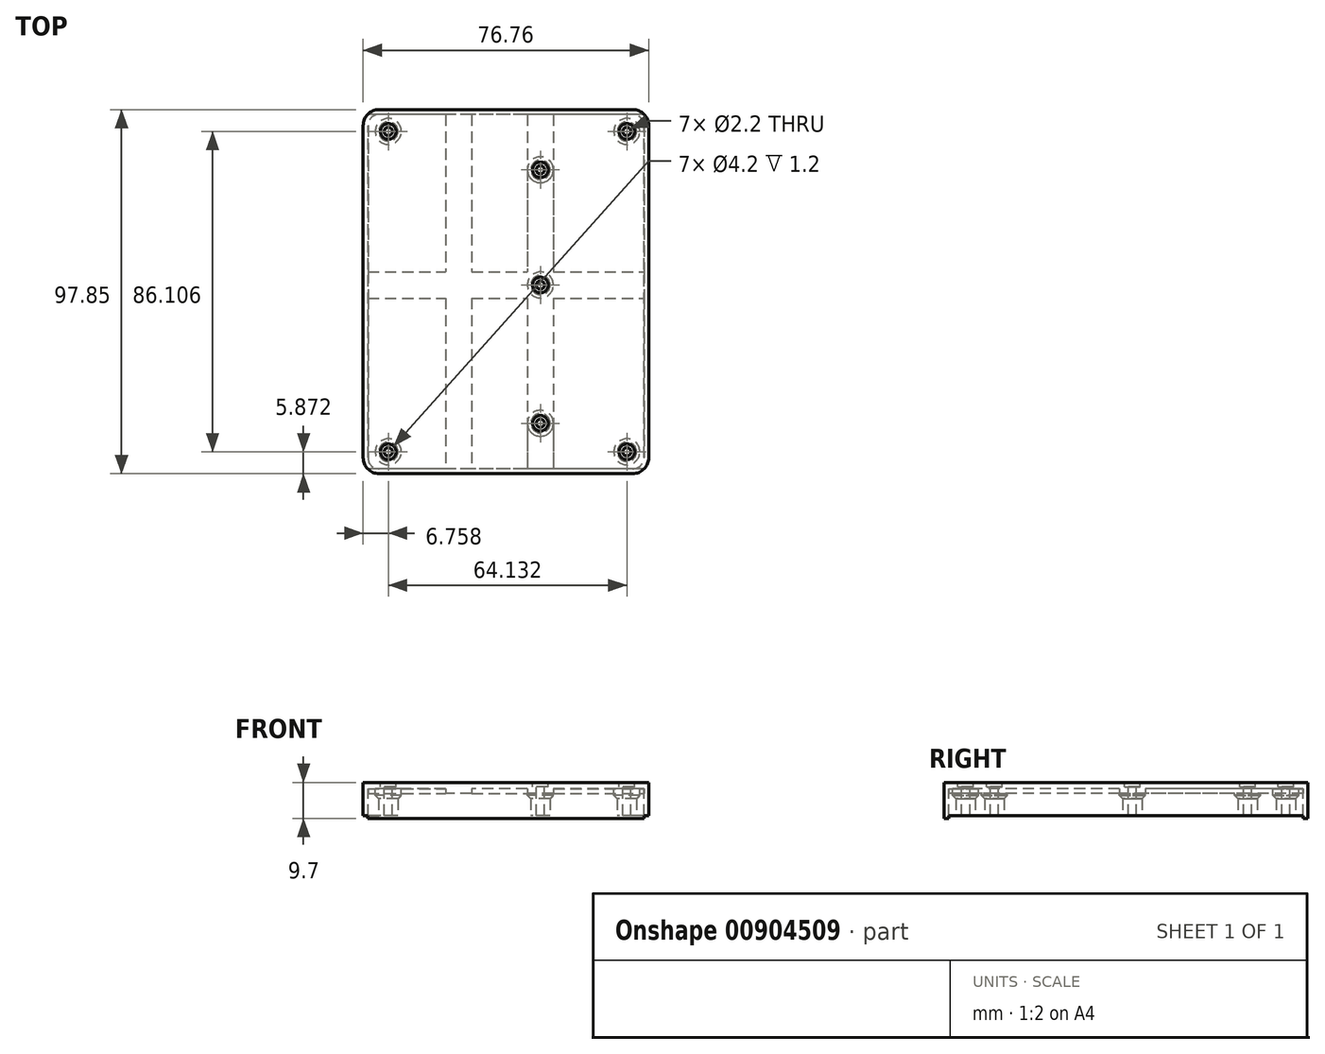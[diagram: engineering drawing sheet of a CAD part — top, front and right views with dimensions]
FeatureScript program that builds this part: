
annotation { "Feature Type Name" : "Feature", "Feature Type Description" : "" }
export const myFeature = defineFeature(function(context is Context, id is Id, definition is map)
    precondition{}
    {
        {
            var Q0;
            Q0=qCreatedBy(makeId("Right.planeOp"),FACE);
            cPlane(context, id + "F0", {"entities" : qUnion([Q0]), "cplaneType" : CPlaneType.OFFSET, "offset" : 9.15 * mm, "width" : 150 * mm, "height" : 150 * mm});
        }
        {
            var Q0;
            Q0=qCreatedBy(makeId("Right.planeOp"),FACE);
            cPlane(context, id + "F1", {"entities" : qUnion([Q0]), "cplaneType" : CPlaneType.OFFSET, "offset" : 83.31 * mm, "width" : 150 * mm, "height" : 150 * mm});
        }
        {
            var Q0;
            Q0=qCreatedBy(makeId("Front.planeOp"),FACE);
            cPlane(context, id + "F2", {"entities" : qUnion([Q0]), "cplaneType" : CPlaneType.OFFSET, "offset" : 95.25 * mm, "oppositeDirection" : true, "width" : 150 * mm, "height" : 150 * mm});
        }
        {
            var Q0;
            Q0=qCreatedBy(makeId("Top.planeOp"),FACE);
            cPlane(context, id + "F3", {"entities" : qUnion([Q0]), "cplaneType" : CPlaneType.OFFSET, "offset" : 1.7 * mm, "width" : 150 * mm, "height" : 150 * mm});
        }
        {
            var Q0;
            Q0=qCreatedBy(id+"F3.planeOp",FACE);
            var sketch = newSketch(context, id + "F4", { "sketchPlane" : qUnion([Q0])});
            skLineSegment(sketch, "E0", {"start": v(83.31, 92.25) * mm, "end": v(83.31, 3) * mm, "construction": true});
            skLineSegment(sketch, "E1", {"start": v(80.31, 95.25) * mm, "end": v(12.15, 95.25) * mm, "construction": true});
            skLineSegment(sketch, "E2", {"start": v(9.15, 92.25) * mm, "end": v(9.15, 3) * mm, "construction": true});
            skLineSegment(sketch, "E3", {"start": v(80.31, 0) * mm, "end": v(12.15, 0) * mm, "construction": true});
            skPoint(sketch, "E4.visualSharp", {"position": v(83.31, 0) * mm});
            skArc(sketch, "E4.filletArc", {"start": v(80.31, 0) * mm, "mid": v(82.43, 0.88) * mm, "end": v(83.31, 3) * mm, "construction": true});
            skPoint(sketch, "E5.visualSharp", {"position": v(83.31, 95.25) * mm});
            skArc(sketch, "E5.filletArc", {"start": v(83.31, 92.25) * mm, "mid": v(82.43, 94.37) * mm, "end": v(80.31, 95.25) * mm, "construction": true});
            skPoint(sketch, "E6.visualSharp", {"position": v(9.15, 95.25) * mm});
            skArc(sketch, "E6.filletArc", {"start": v(12.15, 95.25) * mm, "mid": v(10.03, 94.37) * mm, "end": v(9.15, 92.25) * mm, "construction": true});
            skPoint(sketch, "E7.visualSharp", {"position": v(9.15, 0) * mm});
            skArc(sketch, "E7.filletArc", {"start": v(9.15, 3) * mm, "mid": v(10.03, 0.88) * mm, "end": v(12.15, 0) * mm, "construction": true});
            skArc(sketch, "E8.0", {"start": v(84.61, 92.25) * mm, "mid": v(83.35, 95.3) * mm, "end": v(80.31, 96.55) * mm});
            skLineSegment(sketch, "E8.1", {"start": v(80.31, 96.55) * mm, "end": v(12.15, 96.55) * mm});
            skLineSegment(sketch, "E8.2", {"start": v(84.61, 92.25) * mm, "end": v(84.61, 3) * mm});
            skArc(sketch, "E8.3", {"start": v(12.15, 96.55) * mm, "mid": v(9.1, 95.3) * mm, "end": v(7.85, 92.25) * mm});
            skArc(sketch, "E8.4", {"start": v(80.31, -1.3) * mm, "mid": v(83.35, -0.04) * mm, "end": v(84.61, 3) * mm});
            skLineSegment(sketch, "E8.5", {"start": v(80.31, -1.3) * mm, "end": v(12.15, -1.3) * mm});
            skArc(sketch, "E8.6", {"start": v(7.85, 3) * mm, "mid": v(9.1, -0.04) * mm, "end": v(12.15, -1.3) * mm});
            skLineSegment(sketch, "E8.7", {"start": v(7.85, 92.25) * mm, "end": v(7.85, 3) * mm});
            skSolve(sketch);
        }
        {
            var Q0;
            Q0=qCreatedBy(id+"F3.planeOp",FACE);
            cPlane(context, id + "F5", {"entities" : qUnion([Q0]), "cplaneType" : CPlaneType.OFFSET, "offset" : 5.9 * mm, "width" : 150 * mm, "height" : 150 * mm});
        }
        {
            var Q0;
            Q0=qCreatedBy(id+"F5.planeOp",FACE);
            cPlane(context, id + "F6", {"entities" : qUnion([Q0]), "cplaneType" : CPlaneType.OFFSET, "offset" : 3 * mm, "width" : 150 * mm, "height" : 150 * mm});
        }
        {
            var Q0;
            Q0=makeQuery(id+"F4.imprint","IMPRINT",FACE,{"disambiguationData":[TD([[makeQuery(id+"F4.imprint","IMPRINT",EDGE,{"derivedFrom":sQuery(id+"F4.wireOp",EDGE,"E8.0")}),1.0]])]});
            var Q1;
            Q1=qCreatedBy(id+"F6.planeOp",FACE);
            extrude(context, id + "F7", {"entities" : qUnion([Q0]), "endBound" : BoundingType.UP_TO_SURFACE, "depth" : 25 * mm, "endBoundEntityFace" : qUnion([Q1]), "offsetDistance" : 25 * mm});
        }
        {
            var Q0;
            Q0=qCreatedBy(id+"F3.planeOp",FACE);
            var sketch = newSketch(context, id + "F8", { "sketchPlane" : qUnion([Q0])});
            skLineSegment(sketch, "E9.0", {"start": v(83.31, 92.25) * mm, "end": v(83.31, 3) * mm});
            skArc(sketch, "E10.0", {"start": v(83.31, 92.25) * mm, "mid": v(82.43, 94.37) * mm, "end": v(80.31, 95.25) * mm});
            skLineSegment(sketch, "E11.0", {"start": v(80.31, 95.25) * mm, "end": v(12.15, 95.25) * mm});
            skArc(sketch, "E12.0", {"start": v(12.15, 95.25) * mm, "mid": v(10.03, 94.37) * mm, "end": v(9.15, 92.25) * mm});
            skLineSegment(sketch, "E13.0", {"start": v(9.15, 92.25) * mm, "end": v(9.15, 3) * mm});
            skArc(sketch, "E14.0", {"start": v(9.15, 3) * mm, "mid": v(10.03, 0.88) * mm, "end": v(12.15, 0) * mm});
            skLineSegment(sketch, "E15.0", {"start": v(80.31, 0) * mm, "end": v(12.15, 0) * mm});
            skArc(sketch, "E16.0", {"start": v(80.31, 0) * mm, "mid": v(82.43, 0.88) * mm, "end": v(83.31, 3) * mm});
            skLineSegment(sketch, "E17.0", {"start": v(84.61, 92.25) * mm, "end": v(84.61, 3) * mm});
            skArc(sketch, "E18.0", {"start": v(84.61, 92.25) * mm, "mid": v(83.35, 95.3) * mm, "end": v(80.31, 96.55) * mm});
            skLineSegment(sketch, "E19.0", {"start": v(80.31, 96.55) * mm, "end": v(12.15, 96.55) * mm});
            skArc(sketch, "E20.0", {"start": v(12.15, 96.55) * mm, "mid": v(9.1, 95.3) * mm, "end": v(7.85, 92.25) * mm});
            skLineSegment(sketch, "E21.0", {"start": v(7.85, 92.25) * mm, "end": v(7.85, 3) * mm});
            skArc(sketch, "E22.0", {"start": v(7.85, 3) * mm, "mid": v(9.1, -0.04) * mm, "end": v(12.15, -1.3) * mm});
            skLineSegment(sketch, "E23.0", {"start": v(80.31, -1.3) * mm, "end": v(12.15, -1.3) * mm});
            skArc(sketch, "E24.0", {"start": v(80.31, -1.3) * mm, "mid": v(83.35, -0.04) * mm, "end": v(84.61, 3) * mm});
            skSolve(sketch);
        }
        {
            var Q0;
            Q0=makeQuery(id+"F8.imprint","IMPRINT",FACE,{"disambiguationData":[TD([[makeQuery(id+"F8.imprint","IMPRINT",EDGE,{"derivedFrom":sQuery(id+"F8.wireOp",EDGE,"E9.0")}),1.0]])]});
            extrude(context, id + "F9", {"entities" : qUnion([Q0]), "operationType" : NewBodyOperationType.ADD, "oppositeDirection" : true, "depth" : 0.8 * mm, "offsetDistance" : 25 * mm});
        }
        {
            var Q0;
            Q0=qCreatedBy(id+"F3.planeOp",FACE);
            var sketch = newSketch(context, id + "F10", { "sketchPlane" : qUnion([Q0])});
            skLineSegment(sketch, "E25", {"start": v(14.6, 103.08) * mm, "end": v(14.6, -6.92) * mm, "construction": true});
            skLineSegment(sketch, "E26.0", {"start": v(55.5, 103.08) * mm, "end": v(55.5, -6.92) * mm, "construction": true});
            skLineSegment(sketch, "E27.0", {"start": v(78.74, 103.08) * mm, "end": v(78.74, -6.92) * mm, "construction": true});
            skLineSegment(sketch, "E28", {"start": v(2.6, 4.57) * mm, "end": v(91.38, 4.57) * mm, "construction": true});
            skLineSegment(sketch, "E29.0", {"start": v(2.6, 90.68) * mm, "end": v(91.38, 90.68) * mm, "construction": true});
            skCircle(sketch, "E30", {"center": v(14.6, 4.57) * mm, "radius": 2.6 * mm});
            skCircle(sketch, "E31", {"center": v(78.74, 4.57) * mm, "radius": 2.6 * mm});
            skCircle(sketch, "E32", {"center": v(78.74, 90.68) * mm, "radius": 2.6 * mm});
            skCircle(sketch, "E33", {"center": v(14.6, 90.68) * mm, "radius": 2.6 * mm});
            skCircle(sketch, "E34", {"center": v(55.5, 80.38) * mm, "radius": 2.6 * mm});
            skCircle(sketch, "E35", {"center": v(55.5, 49.4) * mm, "radius": 2.6 * mm});
            skCircle(sketch, "E36", {"center": v(55.5, 12.25) * mm, "radius": 2.6 * mm});
            skLineSegment(sketch, "E37", {"start": v(3.05, 49.4) * mm, "end": v(97.16, 49.4) * mm, "construction": true});
            skSolve(sketch);
        }
        {
            var Q0;
            Q0=qCreatedBy(id+"F3.planeOp",FACE);
            var sketch = newSketch(context, id + "F11", { "sketchPlane" : qUnion([Q0])});
            skLineSegment(sketch, "E38.0", {"start": v(55.5, 103.08) * mm, "end": v(55.5, -6.92) * mm, "construction": true});
            skLineSegment(sketch, "E39.0", {"start": v(52, 95.25) * mm, "end": v(52, 52.9) * mm});
            skLineSegment(sketch, "E40.0", {"start": v(59, 95.25) * mm, "end": v(59, 52.9) * mm});
            skLineSegment(sketch, "E41.0", {"start": v(80.31, 95.25) * mm, "end": v(59, 95.25) * mm});
            skLineSegment(sketch, "E42.0", {"start": v(9.15, 92.25) * mm, "end": v(9.15, 52.9) * mm});
            skLineSegment(sketch, "E43.0", {"start": v(80.31, 0) * mm, "end": v(59, 0) * mm});
            skLineSegment(sketch, "E44.0", {"start": v(83.31, 92.25) * mm, "end": v(83.31, 52.9) * mm});
            skArc(sketch, "E45.0", {"start": v(80.31, 0) * mm, "mid": v(82.43, 0.88) * mm, "end": v(83.31, 3) * mm});
            skArc(sketch, "E46.0", {"start": v(9.15, 3) * mm, "mid": v(10.03, 0.88) * mm, "end": v(12.15, 0) * mm});
            skArc(sketch, "E47.0", {"start": v(12.15, 95.25) * mm, "mid": v(10.03, 94.37) * mm, "end": v(9.15, 92.25) * mm});
            skArc(sketch, "E48.0", {"start": v(83.31, 92.25) * mm, "mid": v(82.43, 94.37) * mm, "end": v(80.31, 95.25) * mm});
            skLineSegment(sketch, "E49.0", {"start": v(3.05, 49.4) * mm, "end": v(97.16, 49.4) * mm, "construction": true});
            skLineSegment(sketch, "E50.0", {"start": v(9.15, 45.9) * mm, "end": v(30.03, 45.9) * mm});
            skLineSegment(sketch, "E51.0", {"start": v(9.15, 52.9) * mm, "end": v(30.03, 52.9) * mm});
            skLineSegment(sketch, "E52.0", {"start": v(33.53, 103.08) * mm, "end": v(33.53, -6.92) * mm, "construction": true});
            skLineSegment(sketch, "E53.0", {"start": v(30.03, 95.25) * mm, "end": v(30.03, 52.9) * mm});
            skLineSegment(sketch, "E54.0", {"start": v(37.03, 95.25) * mm, "end": v(37.03, 52.9) * mm});
            skLineSegment(sketch, "E55.trimOffspring", {"start": v(59, 52.9) * mm, "end": v(83.31, 52.9) * mm});
            skLineSegment(sketch, "E56.trimOffspring", {"start": v(59, 45.9) * mm, "end": v(83.31, 45.9) * mm});
            skLineSegment(sketch, "E57.trimOffspring", {"start": v(52, 45.9) * mm, "end": v(52, 0) * mm});
            skLineSegment(sketch, "E58.trimOffspring", {"start": v(59, 45.9) * mm, "end": v(59, 0) * mm});
            skLineSegment(sketch, "E59.trimOffspring", {"start": v(30.03, 45.9) * mm, "end": v(30.03, 0) * mm});
            skLineSegment(sketch, "E60.trimOffspring", {"start": v(37.03, 52.9) * mm, "end": v(52, 52.9) * mm});
            skLineSegment(sketch, "E61.trimOffspring", {"start": v(37.03, 45.9) * mm, "end": v(37.03, 0) * mm});
            skLineSegment(sketch, "E62.trimOffspring", {"start": v(37.03, 45.9) * mm, "end": v(52, 45.9) * mm});
            skLineSegment(sketch, "E63.trimOffspring", {"start": v(52, 95.25) * mm, "end": v(37.03, 95.25) * mm});
            skLineSegment(sketch, "E64.trimOffspring", {"start": v(30.03, 95.25) * mm, "end": v(12.15, 95.25) * mm});
            skLineSegment(sketch, "E65.trimOffspring", {"start": v(52, 0) * mm, "end": v(37.03, 0) * mm});
            skLineSegment(sketch, "E66.trimOffspring", {"start": v(30.03, 0) * mm, "end": v(12.15, 0) * mm});
            skLineSegment(sketch, "E67.trimOffspring", {"start": v(9.15, 45.9) * mm, "end": v(9.15, 3) * mm});
            skLineSegment(sketch, "E68.trimOffspring", {"start": v(83.31, 45.9) * mm, "end": v(83.31, 3) * mm});
            skSolve(sketch);
        }
        {
            var Q0;
            Q0=qCreatedBy(id+"F6.planeOp",FACE);
            cPlane(context, id + "F12", {"entities" : qUnion([Q0]), "cplaneType" : CPlaneType.OFFSET, "offset" : 1.7 * mm, "oppositeDirection" : true, "width" : 150 * mm, "height" : 150 * mm});
        }
        {
            var Q0;
            Q0=makeQuery(id+"F11.imprint","IMPRINT",FACE,{"disambiguationData":[TD([[makeQuery(id+"F11.imprint","IMPRINT",EDGE,{"derivedFrom":sQuery(id+"F11.wireOp",EDGE,"E43.0")}),-1.0]])]});
            var Q1;
            Q1=makeQuery(id+"F11.imprint","IMPRINT",FACE,{"disambiguationData":[TD([[makeQuery(id+"F11.imprint","IMPRINT",EDGE,{"derivedFrom":sQuery(id+"F11.wireOp",EDGE,"E57.trimOffspring")}),-1.0]])]});
            var Q2;
            Q2=makeQuery(id+"F11.imprint","IMPRINT",FACE,{"disambiguationData":[TD([[makeQuery(id+"F11.imprint","IMPRINT",EDGE,{"derivedFrom":sQuery(id+"F11.wireOp",EDGE,"E46.0")}),1.0]])]});
            var Q3;
            Q3=makeQuery(id+"F11.imprint","IMPRINT",FACE,{"disambiguationData":[TD([[makeQuery(id+"F11.imprint","IMPRINT",EDGE,{"derivedFrom":sQuery(id+"F11.wireOp",EDGE,"E39.0")}),-1.0]])]});
            var Q4;
            Q4=makeQuery(id+"F11.imprint","IMPRINT",FACE,{"disambiguationData":[TD([[makeQuery(id+"F11.imprint","IMPRINT",EDGE,{"derivedFrom":sQuery(id+"F11.wireOp",EDGE,"E40.0")}),1.0]])]});
            var Q5;
            Q5=makeQuery(id+"F11.imprint","IMPRINT",FACE,{"disambiguationData":[TD([[makeQuery(id+"F11.imprint","IMPRINT",EDGE,{"derivedFrom":sQuery(id+"F11.wireOp",EDGE,"E42.0")}),1.0]])]});
            var Q6;
            Q6=qCreatedBy(id+"F12.planeOp",FACE);
            extrude(context, id + "F13", {"entities" : qUnion([Q0, Q1, Q2, Q3, Q4, Q5]), "operationType" : NewBodyOperationType.REMOVE, "endBound" : BoundingType.UP_TO_SURFACE, "depth" : 25 * mm, "endBoundEntityFace" : qUnion([Q6]), "offsetDistance" : 25 * mm});
        }
        {
            var Q0;
            Q0=makeQuery(id+"F8.imprint","IMPRINT",FACE,{"disambiguationData":[TD([[makeQuery(id+"F8.imprint","IMPRINT",EDGE,{"derivedFrom":sQuery(id+"F8.wireOp",EDGE,"E9.0")}),-1.0]])]});
            var Q1;
            Q1=qCreatedBy(id+"F5.planeOp",FACE);
            extrude(context, id + "F14", {"entities" : qUnion([Q0]), "operationType" : NewBodyOperationType.REMOVE, "endBound" : BoundingType.UP_TO_SURFACE, "depth" : 25 * mm, "endBoundEntityFace" : qUnion([Q1]), "offsetDistance" : 25 * mm});
        }
        {
            var Q0;
            Q0=makeQuery(id+"F10.imprint","IMPRINT",FACE,{"disambiguationData":[TD([[makeQuery(id+"F10.imprint","IMPRINT",EDGE,{"derivedFrom":sQuery(id+"F10.wireOp",EDGE,"E32")}),1.0]])]});
            var Q1;
            Q1=makeQuery(id+"F10.imprint","IMPRINT",FACE,{"disambiguationData":[TD([[makeQuery(id+"F10.imprint","IMPRINT",EDGE,{"derivedFrom":sQuery(id+"F10.wireOp",EDGE,"E34")}),1.0]])]});
            var Q2;
            Q2=makeQuery(id+"F10.imprint","IMPRINT",FACE,{"disambiguationData":[TD([[makeQuery(id+"F10.imprint","IMPRINT",EDGE,{"derivedFrom":sQuery(id+"F10.wireOp",EDGE,"E33")}),1.0]])]});
            var Q3;
            Q3=makeQuery(id+"F10.imprint","IMPRINT",FACE,{"disambiguationData":[TD([[makeQuery(id+"F10.imprint","IMPRINT",EDGE,{"derivedFrom":sQuery(id+"F10.wireOp",EDGE,"E35")}),1.0]])]});
            var Q4;
            Q4=makeQuery(id+"F10.imprint","IMPRINT",FACE,{"disambiguationData":[TD([[makeQuery(id+"F10.imprint","IMPRINT",EDGE,{"derivedFrom":sQuery(id+"F10.wireOp",EDGE,"E30")}),1.0]])]});
            var Q5;
            Q5=makeQuery(id+"F10.imprint","IMPRINT",FACE,{"disambiguationData":[TD([[makeQuery(id+"F10.imprint","IMPRINT",EDGE,{"derivedFrom":sQuery(id+"F10.wireOp",EDGE,"E36")}),1.0]])]});
            var Q6;
            Q6=makeQuery(id+"F10.imprint","IMPRINT",FACE,{"disambiguationData":[TD([[makeQuery(id+"F10.imprint","IMPRINT",EDGE,{"derivedFrom":sQuery(id+"F10.wireOp",EDGE,"E31")}),1.0]])]});
            extrude(context, id + "F15", {"entities" : qUnion([Q0, Q1, Q2, Q3, Q4, Q5, Q6]), "operationType" : NewBodyOperationType.ADD, "endBound" : BoundingType.UP_TO_NEXT, "depth" : 25 * mm, "offsetDistance" : 25 * mm});
        }
        {
            var Q0;
            Q0=qCreatedBy(id+"F6.planeOp",FACE);
            var sketch = newSketch(context, id + "F16", { "sketchPlane" : qUnion([Q0])});
            skPoint(sketch, "E69.0", {"position": v(55.5, 12.25) * mm});
            skPoint(sketch, "E70.0", {"position": v(55.5, 49.4) * mm});
            skPoint(sketch, "E71.0", {"position": v(55.5, 80.38) * mm});
            skPoint(sketch, "E72.0", {"position": v(78.74, 90.68) * mm});
            skPoint(sketch, "E73.0", {"position": v(14.6, 90.68) * mm});
            skPoint(sketch, "E74.0", {"position": v(78.74, 4.57) * mm});
            skPoint(sketch, "E75.0", {"position": v(14.6, 4.57) * mm});
            skCircle(sketch, "E76", {"center": v(78.74, 4.57) * mm, "radius": 3.5 * mm});
            skCircle(sketch, "E77", {"center": v(55.5, 12.25) * mm, "radius": 3.5 * mm});
            skCircle(sketch, "E78", {"center": v(14.6, 4.57) * mm, "radius": 3.5 * mm});
            skCircle(sketch, "E79", {"center": v(55.5, 49.4) * mm, "radius": 3.5 * mm});
            skCircle(sketch, "E80", {"center": v(55.5, 80.38) * mm, "radius": 3.5 * mm});
            skCircle(sketch, "E81", {"center": v(14.6, 90.68) * mm, "radius": 3.5 * mm});
            skCircle(sketch, "E82", {"center": v(78.74, 90.68) * mm, "radius": 3.5 * mm});
            skSolve(sketch);
        }
        {
            var Q0;
            Q0=qCreatedBy(id+"F3.planeOp",FACE);
            cPlane(context, id + "F17", {"entities" : qUnion([Q0]), "cplaneType" : CPlaneType.OFFSET, "offset" : 4.5 * mm, "width" : 150 * mm, "height" : 150 * mm});
        }
        {
            var Q0;
            Q0=makeQuery(id+"F16.imprint","IMPRINT",FACE,{"disambiguationData":[TD([[makeQuery(id+"F16.imprint","IMPRINT",EDGE,{"derivedFrom":sQuery(id+"F16.wireOp",EDGE,"E76")}),1.0]])]});
            var Q1;
            Q1=makeQuery(id+"F16.imprint","IMPRINT",FACE,{"disambiguationData":[TD([[makeQuery(id+"F16.imprint","IMPRINT",EDGE,{"derivedFrom":sQuery(id+"F16.wireOp",EDGE,"E82")}),1.0]])]});
            var Q2;
            Q2=makeQuery(id+"F16.imprint","IMPRINT",FACE,{"disambiguationData":[TD([[makeQuery(id+"F16.imprint","IMPRINT",EDGE,{"derivedFrom":sQuery(id+"F16.wireOp",EDGE,"E80")}),1.0]])]});
            var Q3;
            Q3=makeQuery(id+"F16.imprint","IMPRINT",FACE,{"disambiguationData":[TD([[makeQuery(id+"F16.imprint","IMPRINT",EDGE,{"derivedFrom":sQuery(id+"F16.wireOp",EDGE,"E77")}),1.0]])]});
            var Q4;
            Q4=makeQuery(id+"F16.imprint","IMPRINT",FACE,{"disambiguationData":[TD([[makeQuery(id+"F16.imprint","IMPRINT",EDGE,{"derivedFrom":sQuery(id+"F16.wireOp",EDGE,"E81")}),1.0]])]});
            var Q5;
            Q5=makeQuery(id+"F16.imprint","IMPRINT",FACE,{"disambiguationData":[TD([[makeQuery(id+"F16.imprint","IMPRINT",EDGE,{"derivedFrom":sQuery(id+"F16.wireOp",EDGE,"E78")}),1.0]])]});
            var Q6;
            Q6=makeQuery(id+"F16.imprint","IMPRINT",FACE,{"disambiguationData":[TD([[makeQuery(id+"F16.imprint","IMPRINT",EDGE,{"derivedFrom":sQuery(id+"F16.wireOp",EDGE,"E79")}),1.0]])]});
            var Q7;
            Q7=qCreatedBy(id+"F17.planeOp",FACE);
            extrude(context, id + "F18", {"entities" : qUnion([Q0, Q1, Q2, Q3, Q4, Q5, Q6]), "operationType" : NewBodyOperationType.ADD, "endBound" : BoundingType.UP_TO_SURFACE, "oppositeDirection" : true, "depth" : 25 * mm, "endBoundEntityFace" : qUnion([Q7]), "offsetDistance" : 25 * mm});
        }
        {
            var Q0;
            Q0=makeQuery(id+"F18.opExtrude","CAP_EDGE",EDGE,{"disambiguationData":[OSD([sQuery(id+"F16.wireOp",EDGE,"E82")])],"isStart":false});
            var Q1;
            Q1=makeQuery(id+"F18.opExtrude","CAP_EDGE",EDGE,{"disambiguationData":[OSD([sQuery(id+"F16.wireOp",EDGE,"E80")])],"isStart":false});
            var Q2;
            Q2=makeQuery(id+"F18.opExtrude","CAP_EDGE",EDGE,{"disambiguationData":[OSD([sQuery(id+"F16.wireOp",EDGE,"E81")])],"isStart":false});
            var Q3;
            Q3=makeQuery(id+"F18.opExtrude","CAP_EDGE",EDGE,{"disambiguationData":[OSD([sQuery(id+"F16.wireOp",EDGE,"E79")])],"isStart":false});
            var Q4;
            Q4=makeQuery(id+"F18.opExtrude","CAP_EDGE",EDGE,{"disambiguationData":[OSD([sQuery(id+"F16.wireOp",EDGE,"E77")])],"isStart":false});
            var Q5;
            Q5=makeQuery(id+"F18.opExtrude","CAP_EDGE",EDGE,{"disambiguationData":[OSD([sQuery(id+"F16.wireOp",EDGE,"E76")])],"isStart":false});
            var Q6;
            Q6=makeQuery(id+"F18.opExtrude","CAP_EDGE",EDGE,{"disambiguationData":[OSD([sQuery(id+"F16.wireOp",EDGE,"E78")])],"isStart":false});
            chamfer(context, id + "F19", {"entities" : qUnion([Q0, Q1, Q2, Q3, Q4, Q5, Q6]), "width" : 0.9 * mm, "tangentPropagation" : true});
        }
        {
            var Q0;
            Q0=sQuery(id+"F16.wireOp",VERTEX,"E72.0");
            var Q1;
            Q1=sQuery(id+"F16.wireOp",VERTEX,"E80.center");
            var Q2;
            Q2=sQuery(id+"F16.wireOp",VERTEX,"E70.0");
            var Q3;
            Q3=sQuery(id+"F16.wireOp",VERTEX,"E73.0");
            var Q4;
            Q4=sQuery(id+"F16.wireOp",VERTEX,"E77.center");
            var Q5;
            Q5=sQuery(id+"F16.wireOp",VERTEX,"E74.0");
            var Q6;
            Q6=sQuery(id+"F16.wireOp",VERTEX,"E78.center");
            var Q7;
            Q7=makeQuery(id+"F7.opExtrude","SWEPT_BODY",BODY,{"disambiguationData":[OSD([sQuery(id+"F4.wireOp",EDGE,"E8.0"),sQuery(id+"F4.wireOp",EDGE,"E8.1"),sQuery(id+"F4.wireOp",EDGE,"E8.2"),sQuery(id+"F4.wireOp",EDGE,"E8.3"),sQuery(id+"F4.wireOp",EDGE,"E8.4"),sQuery(id+"F4.wireOp",EDGE,"E8.5"),sQuery(id+"F4.wireOp",EDGE,"E8.6"),sQuery(id+"F4.wireOp",EDGE,"E8.7")])]});
            hole(context, id + "F20", {"style" : HoleStyle.C_BORE, "endStyle" : HoleEndStyle.THROUGH, "holeDiameter" : 2.2 * mm, "cBoreDiameter" : 4.2 * mm, "cBoreDepth" : 1.2 * mm, "majorDiameter" : 5 * mm, "isTappedThrough" : true, "tappedDepth" : 12 * mm, "tapClearance" : 3, "locations" : qUnion([Q0, Q1, Q2, Q3, Q4, Q5, Q6]), "scope" : qUnion([Q7])});
        }
        {
            var Q0;
            Q0=qCreatedBy(id+"F3.planeOp",FACE);
            var sketch = newSketch(context, id + "F21", { "sketchPlane" : qUnion([Q0])});
            skLineSegment(sketch, "E83", {"start": v(88.31, 0) * mm, "end": v(4.15, 0) * mm});
            skLineSegment(sketch, "E84", {"start": v(88.31, 95.25) * mm, "end": v(4.15, 95.25) * mm});
            skLineSegment(sketch, "E85", {"start": v(83.31, 95.25) * mm, "end": v(83.31, 0) * mm, "construction": true});
            skLineSegment(sketch, "E86", {"start": v(9.15, 95.25) * mm, "end": v(9.15, 0) * mm, "construction": true});
            skLineSegment(sketch, "E87.0", {"start": v(88.31, 95.25) * mm, "end": v(88.31, 0) * mm});
            skLineSegment(sketch, "E88.0", {"start": v(4.15, 95.25) * mm, "end": v(4.15, 0) * mm});
            skSolve(sketch);
        }
        {
            var Q0;
            Q0=makeQuery(id+"F21.imprint","IMPRINT",FACE,{"disambiguationData":[TD([[makeQuery(id+"F21.imprint","IMPRINT",EDGE,{"derivedFrom":sQuery(id+"F21.wireOp",EDGE,"E83")}),-1.0]])]});
            var Q1;
            Q1=qCreatedBy(makeId("Top.planeOp"),FACE);
            extrude(context, id + "F22", {"entities" : qUnion([Q0]), "operationType" : NewBodyOperationType.REMOVE, "endBound" : BoundingType.THROUGH_ALL, "oppositeDirection" : true, "depth" : 25 * mm, "endBoundEntityFace" : qUnion([Q1]), "offsetDistance" : 25 * mm});
        }
    });
